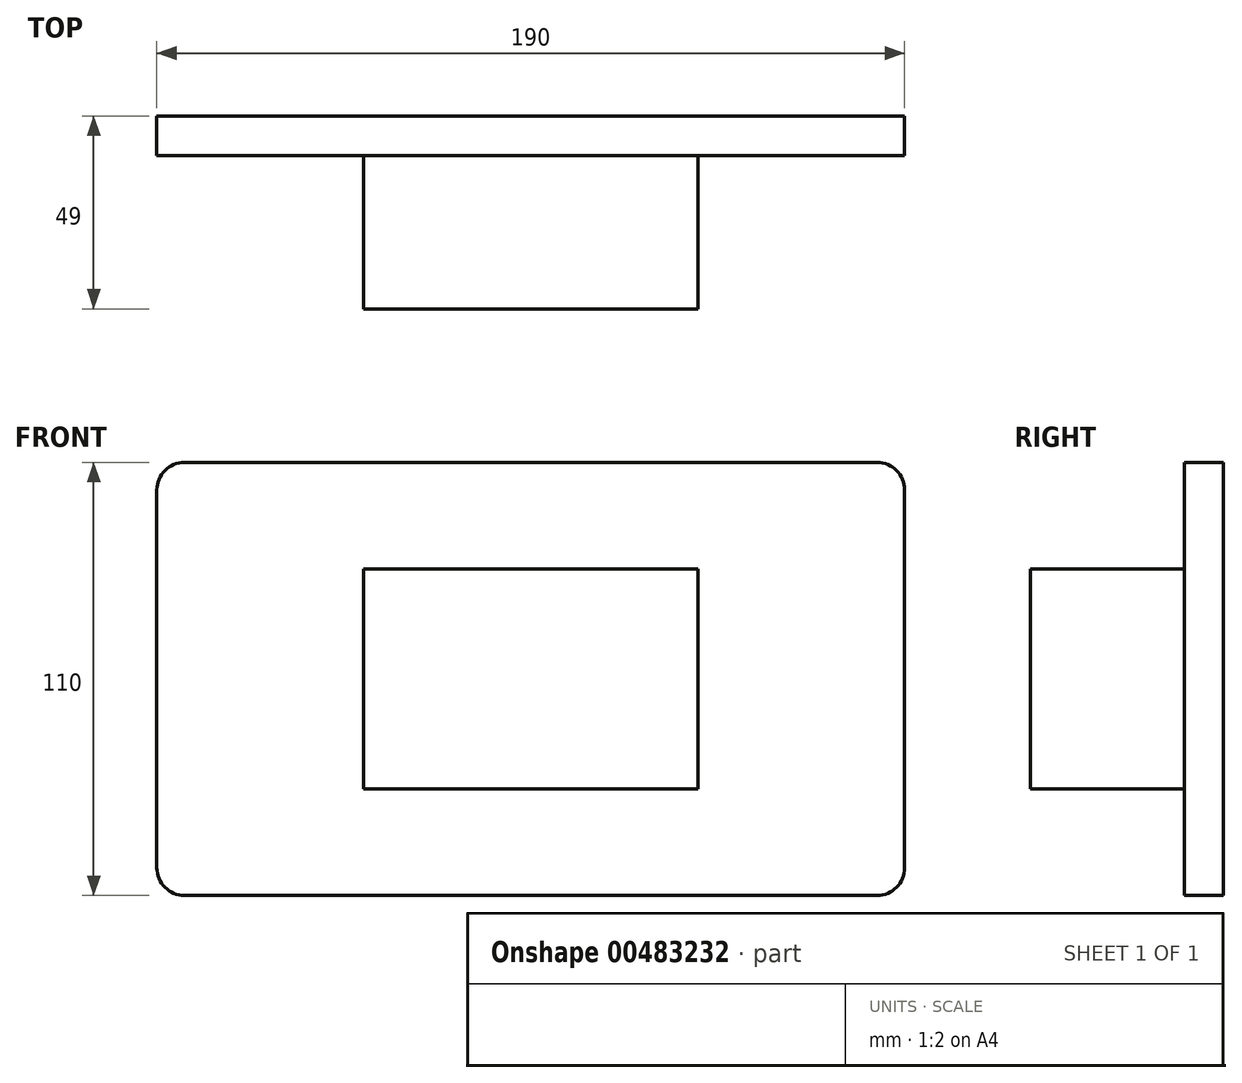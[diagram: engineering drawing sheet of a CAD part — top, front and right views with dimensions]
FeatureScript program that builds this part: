
annotation { "Feature Type Name" : "Feature", "Feature Type Description" : "" }
export const myFeature = defineFeature(function(context is Context, id is Id, definition is map)
    precondition{}
    {
        {
            var Q0;
            Q0=qCreatedBy(makeId("Front.planeOp"),FACE);
            var sketch = newSketch(context, id + "F0", { "sketchPlane" : qUnion([Q0])});
            skLineSegment(sketch, "E0.bottom", {"start": v(87.99, 55) * mm, "end": v(-87.99, 55) * mm});
            skLineSegment(sketch, "E0.top", {"start": v(87.99, -55) * mm, "end": v(-87.99, -55) * mm});
            skLineSegment(sketch, "E0.left", {"start": v(95, 47.99) * mm, "end": v(95, -47.99) * mm});
            skLineSegment(sketch, "E0.right", {"start": v(-95, 47.99) * mm, "end": v(-95, -47.99) * mm});
            skPoint(sketch, "E0.middle", {"position": v(0, 0) * mm});
            skPoint(sketch, "E1.visualSharp", {"position": v(95, 55) * mm});
            skArc(sketch, "E1.filletArc", {"start": v(95, 47.99) * mm, "mid": v(92.95, 52.95) * mm, "end": v(87.99, 55) * mm});
            skPoint(sketch, "E2.visualSharp", {"position": v(-95, 55) * mm});
            skArc(sketch, "E2.filletArc", {"start": v(-87.99, 55) * mm, "mid": v(-92.95, 52.95) * mm, "end": v(-95, 47.99) * mm});
            skPoint(sketch, "E3.visualSharp", {"position": v(-95, -55) * mm});
            skArc(sketch, "E3.filletArc", {"start": v(-95, -47.99) * mm, "mid": v(-92.95, -52.95) * mm, "end": v(-87.99, -55) * mm});
            skPoint(sketch, "E4.visualSharp", {"position": v(95, -55) * mm});
            skArc(sketch, "E4.filletArc", {"start": v(87.99, -55) * mm, "mid": v(92.95, -52.95) * mm, "end": v(95, -47.99) * mm});
            skSolve(sketch);
        }
        {
            var Q0;
            Q0 = qSketchRegion(id + "F0", true);
            extrude(context, id + "F1", {"entities" : qUnion([Q0]), "depth" : 10 * mm});
        }
        {
            var Q0;
            Q0=makeQuery(id+"F1.opExtrude","CAP_FACE",FACE,{"disambiguationData":[OSD([sQuery(id+"F0.wireOp",EDGE,"E0.bottom"),sQuery(id+"F0.wireOp",EDGE,"E0.top"),sQuery(id+"F0.wireOp",EDGE,"E0.left"),sQuery(id+"F0.wireOp",EDGE,"E0.right")])],"isStart":false});
            var sketch = newSketch(context, id + "F2", { "sketchPlane" : qUnion([Q0])});
            skLineSegment(sketch, "E5.bottom", {"start": v(42.5, 28) * mm, "end": v(-42.5, 28) * mm});
            skLineSegment(sketch, "E5.top", {"start": v(42.5, -28) * mm, "end": v(-42.5, -28) * mm});
            skLineSegment(sketch, "E5.left", {"start": v(42.5, 28) * mm, "end": v(42.5, -28) * mm});
            skLineSegment(sketch, "E5.right", {"start": v(-42.5, 28) * mm, "end": v(-42.5, -28) * mm});
            skPoint(sketch, "E5.middle", {"position": v(0, 0) * mm});
            skSolve(sketch);
        }
        {
            var Q0;
            Q0 = qSketchRegion(id + "F2", true);
            extrude(context, id + "F3", {"entities" : qUnion([Q0]), "depth" : 39 * mm});
        }
    });
